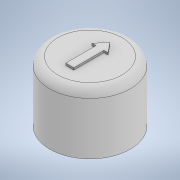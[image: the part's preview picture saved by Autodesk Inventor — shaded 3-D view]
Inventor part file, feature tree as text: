
AUTODESK INVENTOR PART (.ipt)
format: ipt  version: 2021 (Build 250183000, 183)  size: 133,120 bytes
history: native  units: in
note: dims shown in document units (in); Inventor stores cm internally (conversion verified against a paired STEP export)
features: extrude x3, sketch x3, fillet x1
ambient origin geometry x8: Origin, YZ Plane, XZ Plane, XY Plane, X Axis, Y Axis, Z Axis, Center Point
bodies: Solid1 (feature_tree)
feature tree (7):
  extrude  "Extrusion1"  Depth=0.5906in TaperAngle=0.0deg
  extrude  "Extrusion2"  Depth=0.1969in TaperAngle=0.0deg
  fillet  "Fillet1"  Radius=0.0787in
  extrude  "Extrusion3"  Depth=0.2953in
  sketch  "Sketch1"  dims[d0=0.7874in d1=0.5906in d2=0.0in]
  sketch  "Sketch2"  dims[d3=0.5906in d4=0.1969in d5=0.0in d6=0.0787in]
  sketch  "Sketch3"  dims[d7=0.0394in d8=0.2953in d9=0.3937in d10=0.0197in d11=0.0in]
